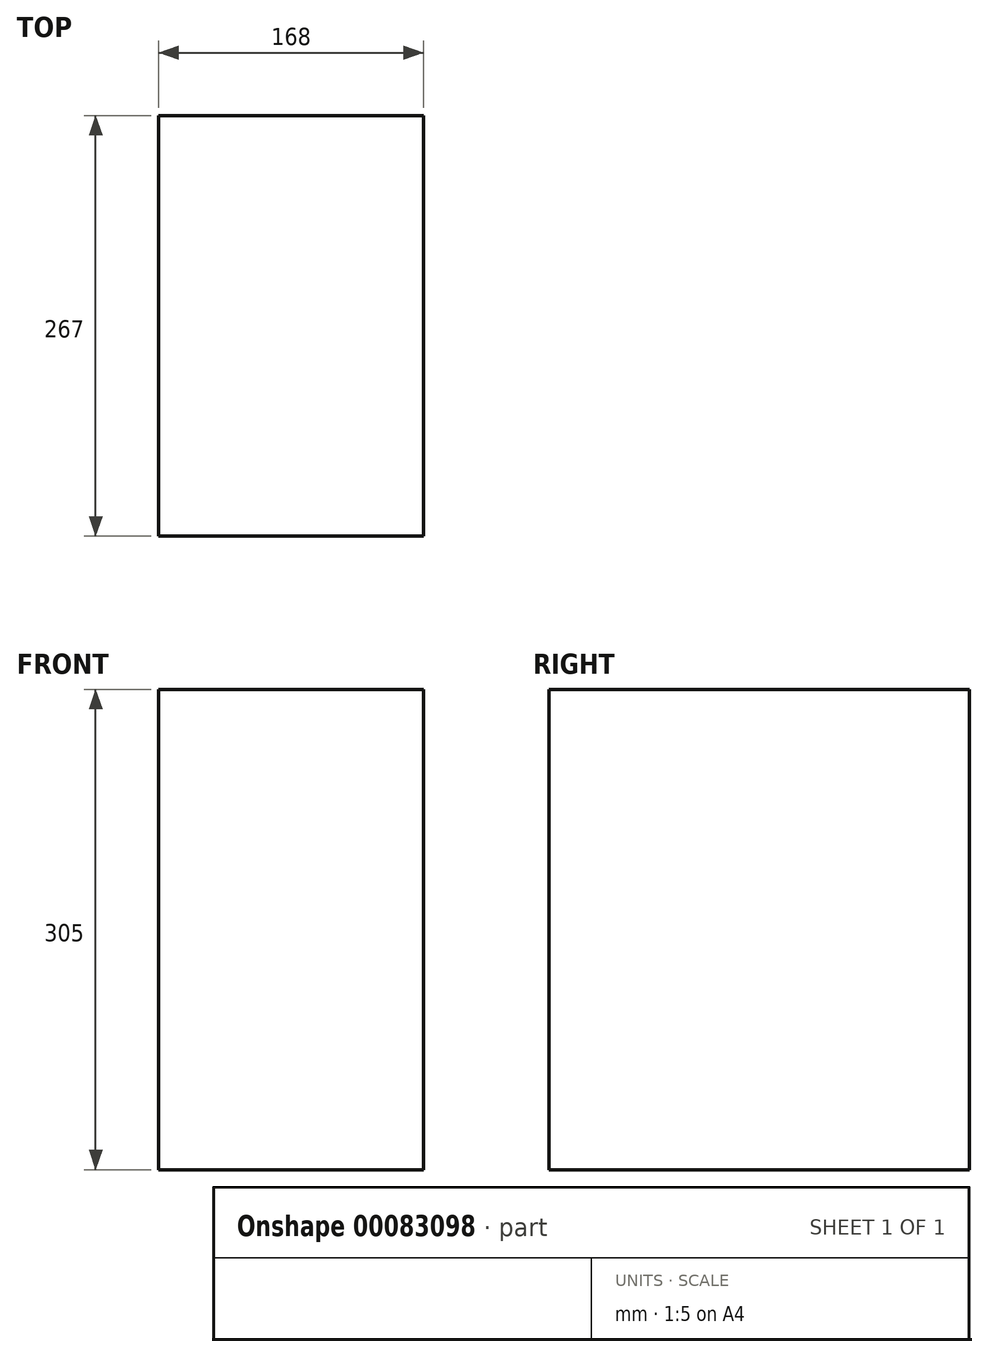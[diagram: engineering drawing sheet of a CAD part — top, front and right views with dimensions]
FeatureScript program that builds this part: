
annotation { "Feature Type Name" : "Feature", "Feature Type Description" : "" }
export const myFeature = defineFeature(function(context is Context, id is Id, definition is map)
    precondition{}
    {
        {
            var Q0;
            Q0=qCreatedBy(makeId("Front.planeOp"),FACE);
            var sketch = newSketch(context, id + "F0", { "sketchPlane" : qUnion([Q0])});
            skLineSegment(sketch, "E0.bottom", {"start": v(0, 0) * mm, "end": v(168, 0) * mm});
            skLineSegment(sketch, "E0.top", {"start": v(0, 305) * mm, "end": v(168, 305) * mm});
            skLineSegment(sketch, "E0.left", {"start": v(0, 0) * mm, "end": v(0, 305) * mm});
            skLineSegment(sketch, "E0.right", {"start": v(168, 0) * mm, "end": v(168, 305) * mm});
            skSolve(sketch);
        }
        {
            var Q0;
            Q0 = qSketchRegion(id + "F0", true);
            var Q1;
            Q1=makeQuery(id+"F0.imprint","IMPRINT",FACE,{"disambiguationData":[TD([[makeQuery(id+"F0.imprint","IMPRINT",EDGE,{"derivedFrom":sQuery(id+"F0.wireOp",EDGE,"E0.bottom")}),1.0]])]});
            extrude(context, id + "F1", {"entities" : qUnion([Q0, Q1]), "depth" : 267 * mm});
        }
    });
